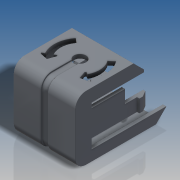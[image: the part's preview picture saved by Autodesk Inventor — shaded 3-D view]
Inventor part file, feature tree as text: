
AUTODESK INVENTOR PART (.ipt)
format: ipt  version: 2016 SP2 (Build 200236200, 236)  size: 547,840 bytes
history: native  units: in
note: dims shown in document units (in); Inventor stores cm internally (conversion verified against a paired STEP export)
features: extrude x7, sketch x3, fillet x1, projected_geometry x1
ambient origin geometry x8: Origin, YZ Plane, XZ Plane, XY Plane, X Axis, Y Axis, Z Axis, Center Point
bodies: Solid1 (feature_tree)
feature tree (12):
  sketch  "Sketch2"  dims[d0=0.8504in d1=0.1417in]
  extrude  "Extrusion1"  Depth=0.1417in
  extrude  "Extrusion2"  Depth=0.2205in
  extrude  "Extrusion3"  Depth=0.0039in
  extrude  "Extrusion4"  Depth=0.0039in
  extrude  "Extrusion5"  Depth=0.0039in
  extrude  "Extrusion6"  Depth=0.0039in
  extrude  "Extrusion7"  Depth=0.0315in
  fillet  "Fillet1"  Radius=0.9134in
  sketch  "Sketch3"  dims[d2=1.2126in d3=0.2205in]
  projected_geometry  "Projected Loop1"
  sketch  "Sketch4"  dims[d4=45.0deg d5=0.1417in d6=0.1732in d7=0.1732in d8=0.1732in d9=0.0315in d10=0.9134in d11=0.063in d12=0.6614in d13=0.8189in d14=0.0567in d15=0.0472in d16=0.063in d17=0.0315in d18=0.0157in d19=0.4724in d20=0.4882in d21=0.5669in d22=0.8189in d23=0.0in d24=0.7244in d25=0.0in d26=0.1575in d27=0.0in d28=0.0875in d29=0.0in d30=0.315in d31=0.0in d32=0.126in d33=0.0315in d34=0.0472in d35=0.0315in d36=0.315in d37=0.0in d38=0.1575in d39=0.2725in d40=0.3386in d41=0.2598in d42=0.6755in d43=0.1546in d44=0.0843in d45=0.4752in d46=0.2061in d47=0.1582in d48=0.315in d49=0.0in d50=0.0039in]
